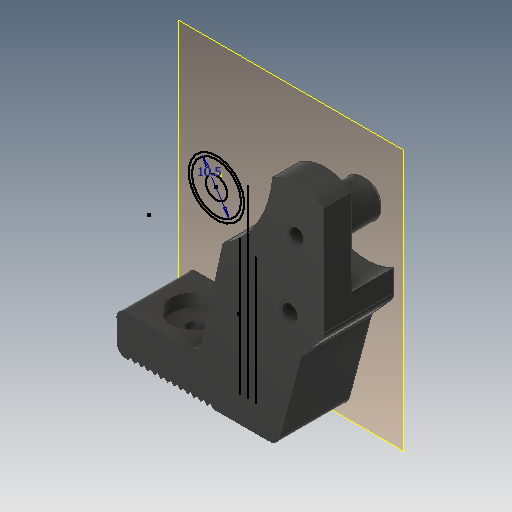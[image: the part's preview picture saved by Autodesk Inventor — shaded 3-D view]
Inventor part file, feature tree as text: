
AUTODESK INVENTOR PART (.ipt)
format: ipt  version: 2017 (Build 210142000, 142)  size: 334,336 bytes
history: native  units: in
note: dims shown in document units (in); Inventor stores cm internally (conversion verified against a paired STEP export)
features: extrude x10, sketch x10, fillet x2, reference x2, plane x1, chamfer x1, projected_geometry x1, other x1
ambient origin geometry x8: Origin, YZ Plane, XZ Plane, XY Plane, X Axis, Y Axis, Z Axis, Center Point
bodies: Solid1 (feature_tree)
feature tree (28):
  plane  "Work Plane1"
  extrude  "Extrusion1"  Depth=0.0787in
  sketch  "Sketch2"  dims[d2=0.0787in d4=0.126in]
  extrude  "Extrusion2"  Depth=0.126in
  chamfer  "Chamfer1"  Distance=0.0394in
  extrude  "Extrusion3"  Depth=0.0394in
  fillet  "Fillet1"  Radius=0.0394in
  extrude  "Extrusion4"  Depth=0.0394in
  extrude  "Extrusion5"  Depth=0.0394in
  extrude  "Extrusion6"  Depth=0.0394in
  extrude  "Extrusion7"  Depth=0.3937in TaperAngle=0.0deg
  sketch  "Sketch9"  dims[d11=0.0394in]
  fillet  "Fillet2"  Radius=0.9449in
  extrude  "Extrusion8"  Depth=0.3937in
  sketch  "Sketch1"  dims[d0=90.0deg d1=0.0787in]
  sketch  "Sketch3"  dims[d5=0.0394in]
  reference  "Reference9"
  sketch  "Sketch4"  dims[d6=135.0deg]
  reference  "Reference10"
  sketch  "Sketch5"  dims[d7=0.0394in]
  sketch  "Sketch6"  dims[d8=0.0394in]
  sketch  "Sketch7"  dims[d9=0.0394in]
  sketch  "Sketch8"  dims[d10=0.0394in]
  projected_geometry  "Projected Loop1"
  sketch  "Sketch10"  dims[d12=0.0394in d13=0.0394in d14=0.0394in d15=0.0394in d16=0.0394in d17=0.0394in d18=0.0394in d19=0.5906in d20=0.0in d21=0.9449in d22=0.311in d23=0.3543in d24=0.0in d25=0.0394in d26=0.0787in d27=45.0deg d28=0.5118in d29=180.0deg d30=105.0deg d31=0.0787in d32=0.3543in d33=0.0in d34=0.0787in d35=0.185in d36=90.0deg d37=0.0591in d38=0.0591in d39=0.126in d40=0.0591in d41=0.126in d42=0.3543in d43=0.3543in d44=0.0in d45=0.3543in d46=0.2244in d47=0.0in d48=90.0deg d49=0.3937in d50=90.0deg d51=0.0in d52=0.126in d53=0.1181in d54=0.0in d55=0.1181in d56=0.0in d57=0.4134in d58=0.0394in d59=0.1181in d60=0.3937in d61=0.0in]
  other  "<userpath>\OneDrive\Inventor\Beast 3D Printer\Extruder Assembly.iam"
  extrude  "Extruder Assembly.iam"  Depth=0.3937in TaperAngle=0.0deg
  extrude  "ExtruderArmwTensioningholeandadjBearing_fixed:1"  Depth=0.0394in TaperAngle=45.0deg
